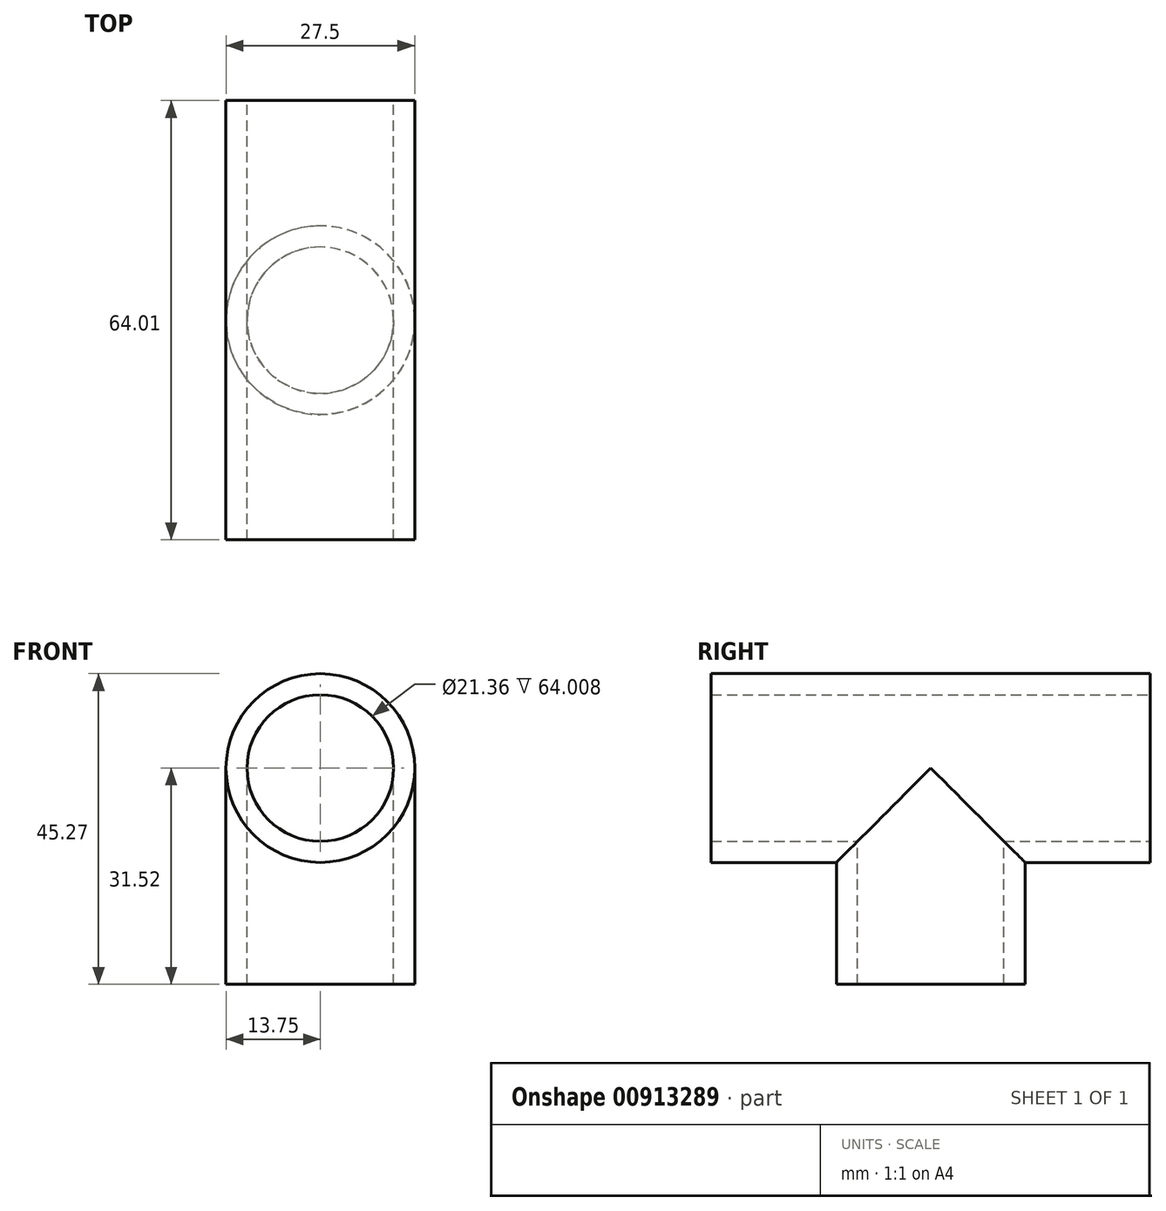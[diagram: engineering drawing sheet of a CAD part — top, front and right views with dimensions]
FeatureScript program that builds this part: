
annotation { "Feature Type Name" : "Feature", "Feature Type Description" : "" }
export const myFeature = defineFeature(function(context is Context, id is Id, definition is map)
    precondition{}
    {
        {
            var Q0;
            Q0=qCreatedBy(makeId("Front.planeOp"),FACE);
            cPlane(context, id + "F0", {"entities" : qUnion([Q0]), "cplaneType" : CPlaneType.OFFSET, "offset" : 31.65 * mm, "width" : 152.4 * mm, "height" : 152.4 * mm});
        }
        {
            var Q0;
            Q0=qCreatedBy(id+"F0.planeOp",FACE);
            var sketch = newSketch(context, id + "F1", { "sketchPlane" : qUnion([Q0])});
            skCircle(sketch, "E0", {"center": v(0, 0) * mm, "radius": 13.75 * mm});
            skCircle(sketch, "E1", {"center": v(0, 0) * mm, "radius": 10.68 * mm});
            skSolve(sketch);
        }
        {
            var Q0;
            Q0=makeQuery(id+"F1.imprint","IMPRINT",FACE,{"disambiguationData":[TD([[makeQuery(id+"F1.imprint","IMPRINT",EDGE,{"derivedFrom":sQuery(id+"F1.wireOp",EDGE,"E0")}),1.0]])]});
            extrude(context, id + "F2", {"entities" : qUnion([Q0]), "depth" : 64 * mm, "offsetDistance" : 25.4 * mm});
        }
        {
            var Q0;
            Q0=qCreatedBy(makeId("Top.planeOp"),FACE);
            var sketch = newSketch(context, id + "F3", { "sketchPlane" : qUnion([Q0])});
            skCircle(sketch, "E2", {"center": v(0, -63.65) * mm, "radius": 13.75 * mm});
            skCircle(sketch, "E3", {"center": v(0, -63.65) * mm, "radius": 10.68 * mm});
            skLineSegment(sketch, "E4.0", {"start": v(13.75, -31.65) * mm, "end": v(-13.75, -31.65) * mm});
            skSolve(sketch);
        }
        {
            var Q0;
            Q0=qSketchRegion(id+"F3",true);
            extrude(context, id + "F4", {"entities" : qUnion([Q0]), "operationType" : NewBodyOperationType.ADD, "oppositeDirection" : true, "depth" : 31.52 * mm, "offsetDistance" : 25.4 * mm});
        }
        {
            var Q0;
            Q0=makeQuery(id+"F1.imprint","IMPRINT",FACE,{"disambiguationData":[TD([[makeQuery(id+"F1.imprint","IMPRINT",EDGE,{"derivedFrom":sQuery(id+"F1.wireOp",EDGE,"E1")}),1.0]])]});
            extrude(context, id + "F5", {"entities" : qUnion([Q0]), "operationType" : NewBodyOperationType.REMOVE, "endBound" : BoundingType.THROUGH_ALL, "depth" : 25.4 * mm, "offsetDistance" : 25.4 * mm});
        }
        {
            var Q0;
            Q0=makeQuery(id+"F3.imprint","IMPRINT",FACE,{"disambiguationData":[TD([[makeQuery(id+"F3.imprint","IMPRINT",EDGE,{"derivedFrom":sQuery(id+"F3.wireOp",EDGE,"E3")}),1.0]])]});
            extrude(context, id + "F6", {"entities" : qUnion([Q0]), "operationType" : NewBodyOperationType.REMOVE, "oppositeDirection" : true, "depth" : 25.4 * mm, "offsetDistance" : 25.4 * mm});
        }
    });
